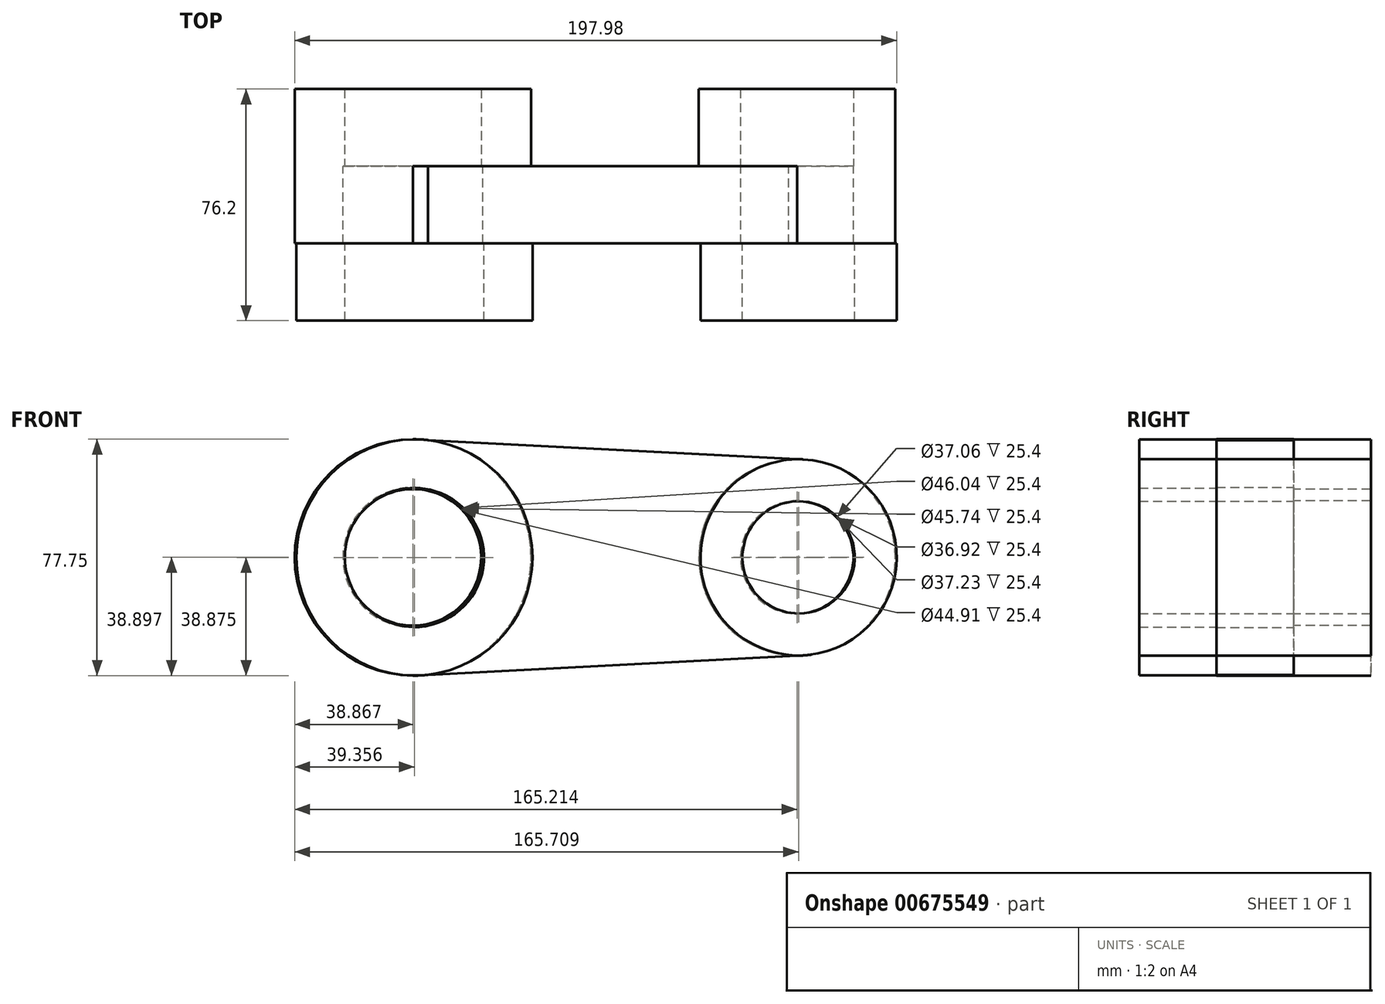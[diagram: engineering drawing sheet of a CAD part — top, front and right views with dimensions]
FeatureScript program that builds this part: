
annotation { "Feature Type Name" : "Feature", "Feature Type Description" : "" }
export const myFeature = defineFeature(function(context is Context, id is Id, definition is map)
    precondition{}
    {
        {
            var Q0;
            Q0=qCreatedBy(makeId("Front.planeOp"),FACE);
            var sketch = newSketch(context, id + "F0", { "sketchPlane" : qUnion([Q0])});
            skCircle(sketch, "E0", {"center": v(-46.2, 13.1) * mm, "radius": 38.87 * mm});
            skCircle(sketch, "E1", {"center": v(-46.2, 13.1) * mm, "radius": 23.02 * mm});
            skCircle(sketch, "E2", {"center": v(80.15, 13.1) * mm, "radius": 32.32 * mm});
            skCircle(sketch, "E3", {"center": v(80.15, 13.1) * mm, "radius": 18.53 * mm});
            skLineSegment(sketch, "E4", {"start": v(-46.2, 51.97) * mm, "end": v(80.15, 45.46) * mm});
            skLineSegment(sketch, "E5", {"start": v(-46.2, -25.78) * mm, "end": v(80.15, -19.22) * mm});
            skArc(sketch, "E6", {"start": v(-46.2, -25.78) * mm, "mid": v(-6.83, 13.1) * mm, "end": v(-46.2, 51.97) * mm});
            skArc(sketch, "E7", {"start": v(80.15, 45.46) * mm, "mid": v(48.3, 13.12) * mm, "end": v(80.15, -19.22) * mm});
            skSolve(sketch);
        }
        {
            var Q0;
            Q0 = qSketchRegion(id + "F0", true);
            extrude(context, id + "F1", {"entities" : qUnion([Q0]), "depth" : 25.4 * mm, "offsetDistance" : 25.4 * mm});
        }
        {
            var Q0;
            Q0=makeQuery(id+"F1.opExtrude","CAP_FACE",FACE,{"disambiguationData":[OSD([sQuery(id+"F0.wireOp",EDGE,"E0"),sQuery(id+"F0.wireOp",EDGE,"E1"),sQuery(id+"F0.wireOp",EDGE,"E2"),sQuery(id+"F0.wireOp",EDGE,"E3"),sQuery(id+"F0.wireOp",EDGE,"E4"),sQuery(id+"F0.wireOp",EDGE,"E5"),sQuery(id+"F0.wireOp",EDGE,"E6"),sQuery(id+"F0.wireOp",EDGE,"E7")])],"isStart":false});
            var sketch = newSketch(context, id + "F2", { "sketchPlane" : qUnion([Q0])});
            skCircle(sketch, "E8", {"center": v(-45.7, 13.1) * mm, "radius": 38.83 * mm});
            skCircle(sketch, "E9", {"center": v(-45.7, 13.1) * mm, "radius": 22.87 * mm});
            skCircle(sketch, "E10", {"center": v(80.65, 13.12) * mm, "radius": 32.27 * mm});
            skCircle(sketch, "E11", {"center": v(80.65, 13.12) * mm, "radius": 18.46 * mm});
            skSolve(sketch);
        }
        {
            var Q0;
            Q0 = qSketchRegion(id + "F2", true);
            extrude(context, id + "F3", {"entities" : qUnion([Q0]), "operationType" : NewBodyOperationType.ADD, "depth" : 25.4 * mm, "offsetDistance" : 25.4 * mm});
        }
        {
            var Q0;
            Q0=makeQuery(id+"F1.opExtrude","CAP_FACE",FACE,{"disambiguationData":[OSD([sQuery(id+"F0.wireOp",EDGE,"E0"),sQuery(id+"F0.wireOp",EDGE,"E1"),sQuery(id+"F0.wireOp",EDGE,"E2"),sQuery(id+"F0.wireOp",EDGE,"E3"),sQuery(id+"F0.wireOp",EDGE,"E4"),sQuery(id+"F0.wireOp",EDGE,"E5"),sQuery(id+"F0.wireOp",EDGE,"E6"),sQuery(id+"F0.wireOp",EDGE,"E7")])],"isStart":true});
            var sketch = newSketch(context, id + "F4", { "sketchPlane" : qUnion([Q0])});
            skCircle(sketch, "E12", {"center": v(-80.15, 13.1) * mm, "radius": 32.32 * mm});
            skCircle(sketch, "E13", {"center": v(-80.15, 13.1) * mm, "radius": 18.62 * mm});
            skCircle(sketch, "E14", {"center": v(46.2, 13.1) * mm, "radius": 38.87 * mm});
            skCircle(sketch, "E15", {"center": v(46.2, 13.1) * mm, "radius": 22.45 * mm});
            skSolve(sketch);
        }
        {
            var Q0;
            Q0 = qSketchRegion(id + "F4", true);
            extrude(context, id + "F5", {"entities" : qUnion([Q0]), "operationType" : NewBodyOperationType.ADD, "depth" : 25.4 * mm, "offsetDistance" : 25.4 * mm});
        }
    });
